# Revit family: Gleitschlitten Typ HV1, m.D., Ø219 bis Ø457mm, h=100mm bis h=155mm_
name_source: partatom
category: HLS-Bauteile
revit_build: Autodesk Revit 2018 (Build: 20190510_1515(x64)
units: mm (PartAtom-declared; Revit-internal decimal feet)

## family parameters
Arbeitsebenenbasiert = Ja
Beim Laden mit Abzugskörper schneiden = Nein
Bemaßung runder Anschluss = Durchmesser verwenden
Gemeinsam genutzt = Ja
Immer vertikal = Nein
Klassifizierung = Keine
Raumberechnungspunkt = Nein
Teiletyp = Normal

## types (11) — shared parameters
Baustoffklasse = B2
Breite Schellenband = 50 mm
Dämmstärke = 6 mm  [stored 0.019685 ft]
Fabrikat = MEFA
Kurztext1 = Gleitschlitten A HV 100-150 50x5
L = 160 mm  [stored 0.524934 ft]
Länge Unterbau = 270 mm
Mengeneinheit = St
Schalldämmeinlage = Gummi EPDM
Sicherheitsfaktor = 1.54
Stärke Schellenband = 5 mm
Verschluss = Mutter / Verschluss-Schraube
Verschluss-Schraube = M12
Vorgabe-Ansicht = 1219 mm
max. Höhe Unterbau = 150 mm
max. Temperaturbeständigkeit = 100 °C
min. Höhe Unterbau = 100 mm
vpe = 1

## per-type parameters (varying)
| type | A (Breite) | Artikelnummer | Breite Unterbau | EAN | Flachmaterial | Gewicht | Gewicht pro Bauteil | Kurztext2 | Rohraußendurchmesser | Schellenteil | Schuh | Stärke Material |
| Gleitschlitten HV1, m.D., Ø219mm, h=100mm bis h=155mm | 140 mm  [stored 0.459318 ft] | 142afb0219 | 256 mm | 4250928462855 | Flachmaterial nach DIN (50-5 und 70-8) für HV1 : für Ø219 | 12.70 kg | 12.70 kg | 219 mm EPDM fsv | 219 mm  [stored 0.718504 ft] | Schellenteil für HV mit RS m.D : Schelleteil für 219 m.D. | TL-Fuß für Gleitschl.2Lo.14 : 9000816 | 6 mm  [stored 0.019685 ft] |
| Gleitschlitten HV1, m.D., Ø225mm, h=100mm bis h=155mm | 140 mm  [stored 0.459318 ft] | 142afb0225 | 256 mm | 4250928462862 | Flachmaterial nach DIN (50-5 und 70-8) für HV1 : für Ø225 | 12.80 kg | 12.80 kg | 225 mm EPDM fsv | 225 mm  [stored 0.738189 ft] | Schellenteil für HV mit RS m.D : Schelleteil für 225 m.D. | TL-Fuß für Gleitschl.2Lo.14 : 9000816 | 6 mm  [stored 0.019685 ft] |
| Gleitschlitten HV1, m.D., Ø273mm, h=100mm bis h=155mm | 172 mm  [stored 0.564304 ft] | 142afb0273 | 288 mm | 4250928462879 | Flachmaterial nach DIN (50-5 und 70-8) für HV1 : für Ø273 | 13.87 kg | 13.87 kg | 273 mm EPDM fsv | 273 mm  [stored 0.895669 ft] | Schellenteil für HV mit RS m.D : Schelleteil für 273 m.D. | TL-Fuß für Gleitschl.2Lo.14 : 9000816 | 6 mm  [stored 0.019685 ft] |
| Gleitschlitten HV1, m.D., Ø280mm, h=100mm bis h=155mm | 172 mm  [stored 0.564304 ft] | 142afb0280 | 288 mm | 4250928462886 | Flachmaterial nach DIN (50-5 und 70-8) für HV1 : für Ø280 | 13.97 kg | 13.97 kg | 280 mm EPDM fsv | 280 mm  [stored 0.918635 ft] | Schellenteil für HV mit RS m.D : Schelleteil für 280 m.D. | TL-Fuß für Gleitschl.2Lo.14 : 9000816 | 6 mm  [stored 0.019685 ft] |
| Gleitschlitten HV1, m.D., Ø315mm, h=100mm bis h=155mm | 172 mm  [stored 0.564304 ft] | 142afb0315 | 288 mm | 4250928462893 | Flachmaterial nach DIN (50-5 und 70-8) für HV1 : für Ø315 | 14.41 kg | 14.41 kg | 315 mm EPDM fsv | 315 mm  [stored 1.03346 ft] | Schellenteil für HV mit RS m.D : Schelleteil für 315 m.D. | TL-Fuß für Gleitschl.2Lo.14 : 9000816 | 6 mm  [stored 0.019685 ft] |
| Gleitschlitten HV1, m.D., Ø324mm, h=100mm bis h=155mm | 172 mm  [stored 0.564304 ft] | 142afb0324 | 288 mm | 4250928462909 | Flachmaterial nach DIN (50-5 und 70-8) für HV1 : für Ø324 | 14.55 kg | 14.55 kg | 324 mm EPDM fsv | 324 mm  [stored 1.06299 ft] | Schellenteil für HV mit RS m.D : Schelleteil für 324 m.D. | TL-Fuß für Gleitschl.2Lo.14 : 9000816 | 6 mm  [stored 0.019685 ft] |
| Gleitschlitten HV1, m.D., Ø356mm, h=100mm bis h=155mm | 172 mm  [stored 0.564304 ft] | 142afb0356 | 288 mm | 4250928462916 | Flachmaterial nach DIN (50-5 und 70-8) für HV1 : für Ø356 | 14.91 kg | 14.91 kg | 356 mm EPDM fsv | 356 mm  [stored 1.16798 ft] | Schellenteil für HV mit RS m.D : Schelleteil für 356 m.D. | TL-Fuß für Gleitschl.2Lo.14 : 9000816 | 6 mm  [stored 0.019685 ft] |
| Gleitschlitten HV1, m.D., Ø400mm, h=100mm bis h=155mm | 225 mm  [stored 0.738189 ft] | 142afb0400 | 341 mm | 4250928462923 | Flachmaterial nach DIN (50-5 und 70-8) für HV1 : für Ø400 | 18.76 kg | 18.76 kg | 400 mm EPDM fsv | 400 mm  [stored 1.31234 ft] | Schellenteil für HV mit RS m.D : Schelleteil für 400 m.D. | TL-Fuß für Gleitschl.2Lo.14 : 9000817 | 8 mm  [stored 0.0262467 ft] |
| Gleitschlitten HV1, m.D., Ø406mm, h=100mm bis h=155mm | 225 mm  [stored 0.738189 ft] | 142afb0406 | 341 mm | 4250928462930 | Flachmaterial nach DIN (50-5 und 70-8) für HV1 : für Ø406.4 | 18.92 kg | 18.92 kg | 406 mm EPDM fsv | 406 mm  [stored 1.33202 ft] | Schellenteil für HV mit RS m.D : Schelleteil für 406 m.D. | TL-Fuß für Gleitschl.2Lo.14 : 9000817 | 8 mm  [stored 0.0262467 ft] |
| Gleitschlitten HV1, m.D., Ø450mm, h=100mm bis h=155mm | 225 mm  [stored 0.738189 ft] | 142afb0450 | 341 mm | 4250928462947 | Flachmaterial nach DIN (50-5 und 70-8) für HV1 : für Ø450 | 19.43 kg | 19.43 kg | 450 mm EPDM fsv | 450 mm  [stored 1.47638 ft] | Schellenteil für HV mit RS m.D : Schelleteil für 450 m.D. | TL-Fuß für Gleitschl.2Lo.14 : 9000817 | 8 mm  [stored 0.0262467 ft] |
| Gleitschlitten HV1, m.D., Ø457mm, h=100mm bis h=155mm | 225 mm  [stored 0.738189 ft] | 142afb0457 | 341 mm | 4250928462954 | Flachmaterial nach DIN (50-5 und 70-8) für HV1 : für Ø457 | 19.75 kg | 19.75 kg | 457 mm EPDM fsv | 457 mm  [stored 1.49934 ft] | Schellenteil für HV mit RS m.D : Schelleteil für 457 m.D. | TL-Fuß für Gleitschl.2Lo.14 : 9000817 | 8 mm  [stored 0.0262467 ft] |

note: [stored X ft] marks values corroborated as IEEE doubles in the binary element streams (Revit-internal decimal feet)

## geometry (parser evidence)
native form markers: Sweep x19
no freeform markers — native parametric forms only
